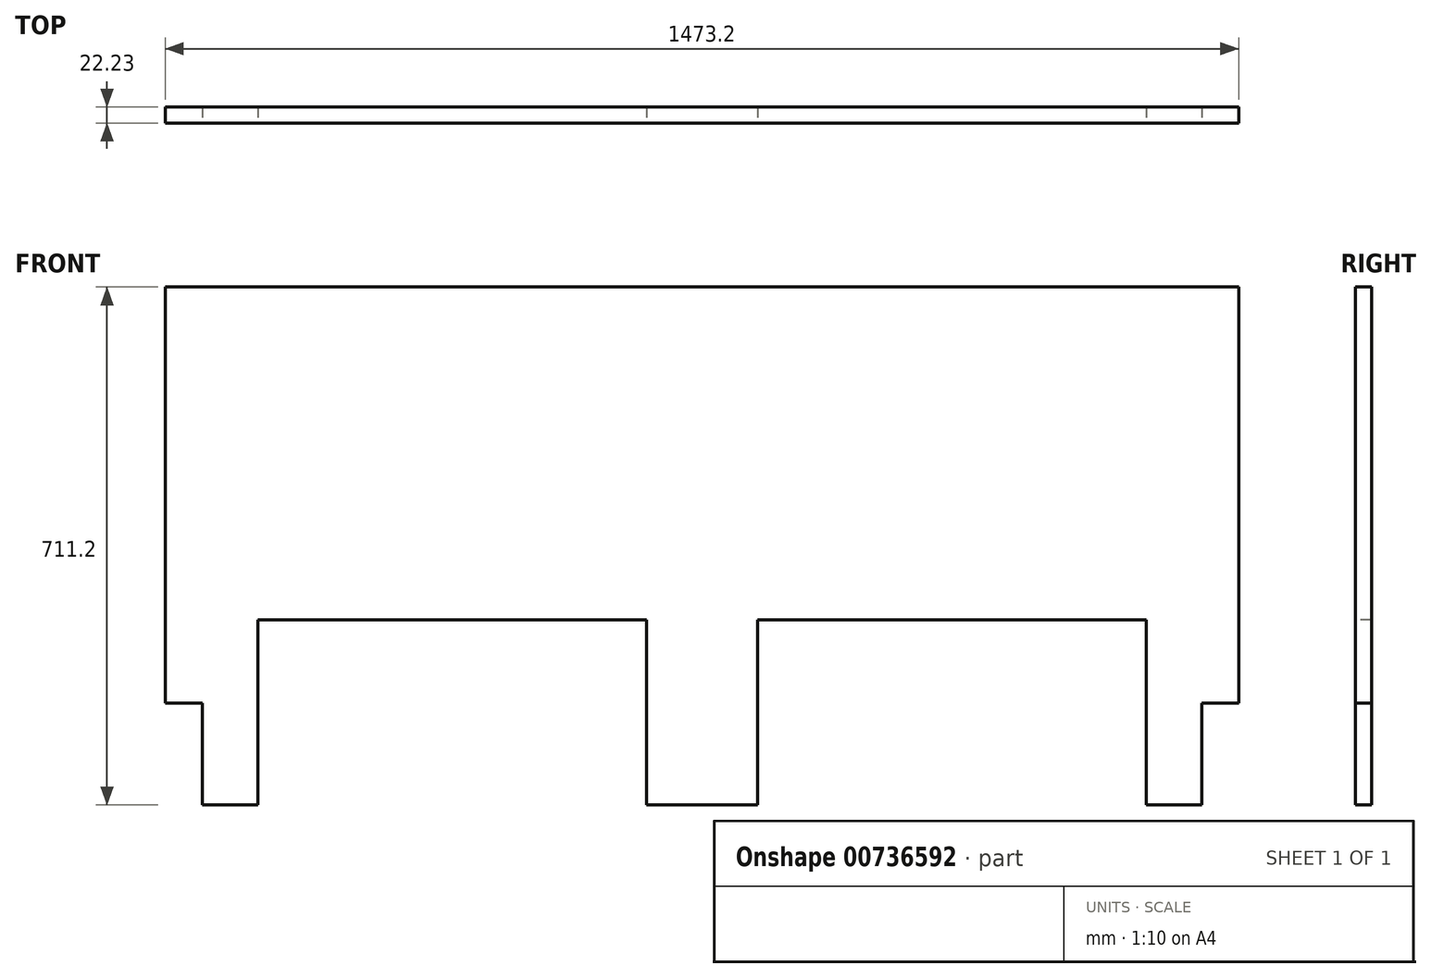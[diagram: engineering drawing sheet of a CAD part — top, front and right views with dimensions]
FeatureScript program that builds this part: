
annotation { "Feature Type Name" : "Feature", "Feature Type Description" : "" }
export const myFeature = defineFeature(function(context is Context, id is Id, definition is map)
    precondition{}
    {
        {
            var Q0;
            Q0=qCreatedBy(makeId("Front.planeOp"),FACE);
            var sketch = newSketch(context, id + "F0", { "sketchPlane" : qUnion([Q0])});
            skLineSegment(sketch, "E0.bottom", {"start": v(-223.68, 711.2) * mm, "end": v(-96.68, 711.2) * mm});
            skLineSegment(sketch, "E0.top", {"start": v(-223.68, 0) * mm, "end": v(-96.68, 0) * mm});
            skLineSegment(sketch, "E0.left", {"start": v(-223.68, 711.2) * mm, "end": v(-223.68, 0) * mm});
            skLineSegment(sketch, "E0.right", {"start": v(-96.68, 711.2) * mm, "end": v(-96.68, 0) * mm});
            skLineSegment(sketch, "E1.bottom", {"start": v(1122.52, 711.2) * mm, "end": v(1249.52, 711.2) * mm});
            skLineSegment(sketch, "E1.top", {"start": v(1122.52, 0) * mm, "end": v(1249.52, 0) * mm});
            skLineSegment(sketch, "E1.left", {"start": v(1122.52, 711.2) * mm, "end": v(1122.52, 0) * mm});
            skLineSegment(sketch, "E1.right", {"start": v(1249.52, 711.2) * mm, "end": v(1249.52, 0) * mm});
            skLineSegment(sketch, "E2.bottom", {"start": v(436.72, 711.2) * mm, "end": v(589.12, 711.2) * mm});
            skLineSegment(sketch, "E2.top", {"start": v(436.72, 0) * mm, "end": v(589.12, 0) * mm});
            skLineSegment(sketch, "E2.left", {"start": v(436.72, 711.2) * mm, "end": v(436.72, 0) * mm});
            skLineSegment(sketch, "E2.right", {"start": v(589.12, 711.2) * mm, "end": v(589.12, 0) * mm});
            skLineSegment(sketch, "E3", {"start": v(512.92, 0) * mm, "end": v(512.92, 711.2) * mm, "construction": true});
            skLineSegment(sketch, "E4.bottom", {"start": v(-96.68, 711.2) * mm, "end": v(436.72, 711.2) * mm});
            skLineSegment(sketch, "E4.top", {"start": v(-96.68, 254) * mm, "end": v(436.72, 254) * mm});
            skLineSegment(sketch, "E4.left", {"start": v(-96.68, 711.2) * mm, "end": v(-96.68, 254) * mm});
            skLineSegment(sketch, "E4.right", {"start": v(436.72, 711.2) * mm, "end": v(436.72, 254) * mm});
            skLineSegment(sketch, "E5.bottom", {"start": v(589.12, 711.2) * mm, "end": v(1122.52, 711.2) * mm});
            skLineSegment(sketch, "E5.top", {"start": v(589.12, 254) * mm, "end": v(1122.52, 254) * mm});
            skLineSegment(sketch, "E5.left", {"start": v(589.12, 711.2) * mm, "end": v(589.12, 254) * mm});
            skLineSegment(sketch, "E5.right", {"start": v(1122.52, 711.2) * mm, "end": v(1122.52, 254) * mm});
            skPoint(sketch, "E6.oppositeSnap0", {"position": v(-98.35, 43.88) * mm});
            skLineSegment(sketch, "E6.bottom", {"start": v(-223.68, 0) * mm, "end": v(-172.88, 0) * mm});
            skLineSegment(sketch, "E6.top", {"start": v(-223.68, 139.7) * mm, "end": v(-172.88, 139.7) * mm});
            skLineSegment(sketch, "E6.left", {"start": v(-223.68, 0) * mm, "end": v(-223.68, 139.7) * mm});
            skLineSegment(sketch, "E6.right", {"start": v(-172.88, 0) * mm, "end": v(-172.88, 139.7) * mm});
            skPoint(sketch, "E7.orphan", {"position": v(-98.35, 139.7) * mm});
            skLineSegment(sketch, "E8.bottom", {"start": v(1249.52, 0) * mm, "end": v(1198.72, 0) * mm});
            skLineSegment(sketch, "E8.top", {"start": v(1249.52, 139.7) * mm, "end": v(1198.72, 139.7) * mm});
            skLineSegment(sketch, "E8.left", {"start": v(1249.52, 0) * mm, "end": v(1249.52, 139.7) * mm});
            skLineSegment(sketch, "E8.right", {"start": v(1198.72, 0) * mm, "end": v(1198.72, 139.7) * mm});
            skSolve(sketch);
        }
        {
            var Q0;
            Q0=makeQuery(id+"F0.imprint","IMPRINT",FACE,{"disambiguationData":[TD([[makeQuery(id+"F0.imprint","IMPRINT",EDGE,{"derivedFrom":sQuery(id+"F0.wireOp",EDGE,"E0.bottom")}),-1.0]])]});
            var Q1;
            Q1=makeQuery(id+"F0.imprint","IMPRINT",FACE,{"disambiguationData":[TD([[makeQuery(id+"F0.imprint","IMPRINT",EDGE,{"derivedFrom":sQuery(id+"F0.wireOp",EDGE,"E4.bottom")}),-1.0]])]});
            var Q2;
            Q2=makeQuery(id+"F0.imprint","IMPRINT",FACE,{"disambiguationData":[TD([[makeQuery(id+"F0.imprint","IMPRINT",EDGE,{"derivedFrom":sQuery(id+"F0.wireOp",EDGE,"E1.bottom")}),-1.0]])]});
            var Q3;
            Q3=makeQuery(id+"F0.imprint","IMPRINT",FACE,{"disambiguationData":[TD([[makeQuery(id+"F0.imprint","IMPRINT",EDGE,{"derivedFrom":sQuery(id+"F0.wireOp",EDGE,"E5.bottom")}),-1.0]])]});
            var Q4;
            Q4=makeQuery(id+"F0.imprint","IMPRINT",FACE,{"disambiguationData":[TD([[makeQuery(id+"F0.imprint","IMPRINT",EDGE,{"derivedFrom":sQuery(id+"F0.wireOp",EDGE,"E2.bottom")}),-1.0]])]});
            extrude(context, id + "F1", {"entities" : qUnion([Q0, Q1, Q2, Q3, Q4]), "oppositeDirection" : true, "depth" : 22.22 * mm, "offsetDistance" : 25.4 * mm});
        }
        {
            var Q0;
            Q0=makeQuery(id+"F0.imprint","IMPRINT",FACE,{"disambiguationData":[TD([[makeQuery(id+"F0.imprint","IMPRINT",EDGE,{"derivedFrom":sQuery(id+"F0.wireOp",EDGE,"E6.bottom")}),1.0]])]});
            var Q1;
            Q1=makeQuery(id+"F0.imprint","IMPRINT",FACE,{"disambiguationData":[TD([[makeQuery(id+"F0.imprint","IMPRINT",EDGE,{"derivedFrom":sQuery(id+"F0.wireOp",EDGE,"E8.bottom")}),-1.0]])]});
            var Q2;
            Q2 = qSketchRegion(id + "F0", true);
            extrude(context, id + "F2", {"entities" : qUnion([Q0, Q1, Q2]), "operationType" : NewBodyOperationType.REMOVE, "depth" : 22.22 * mm, "offsetDistance" : 25.4 * mm});
        }
    });
